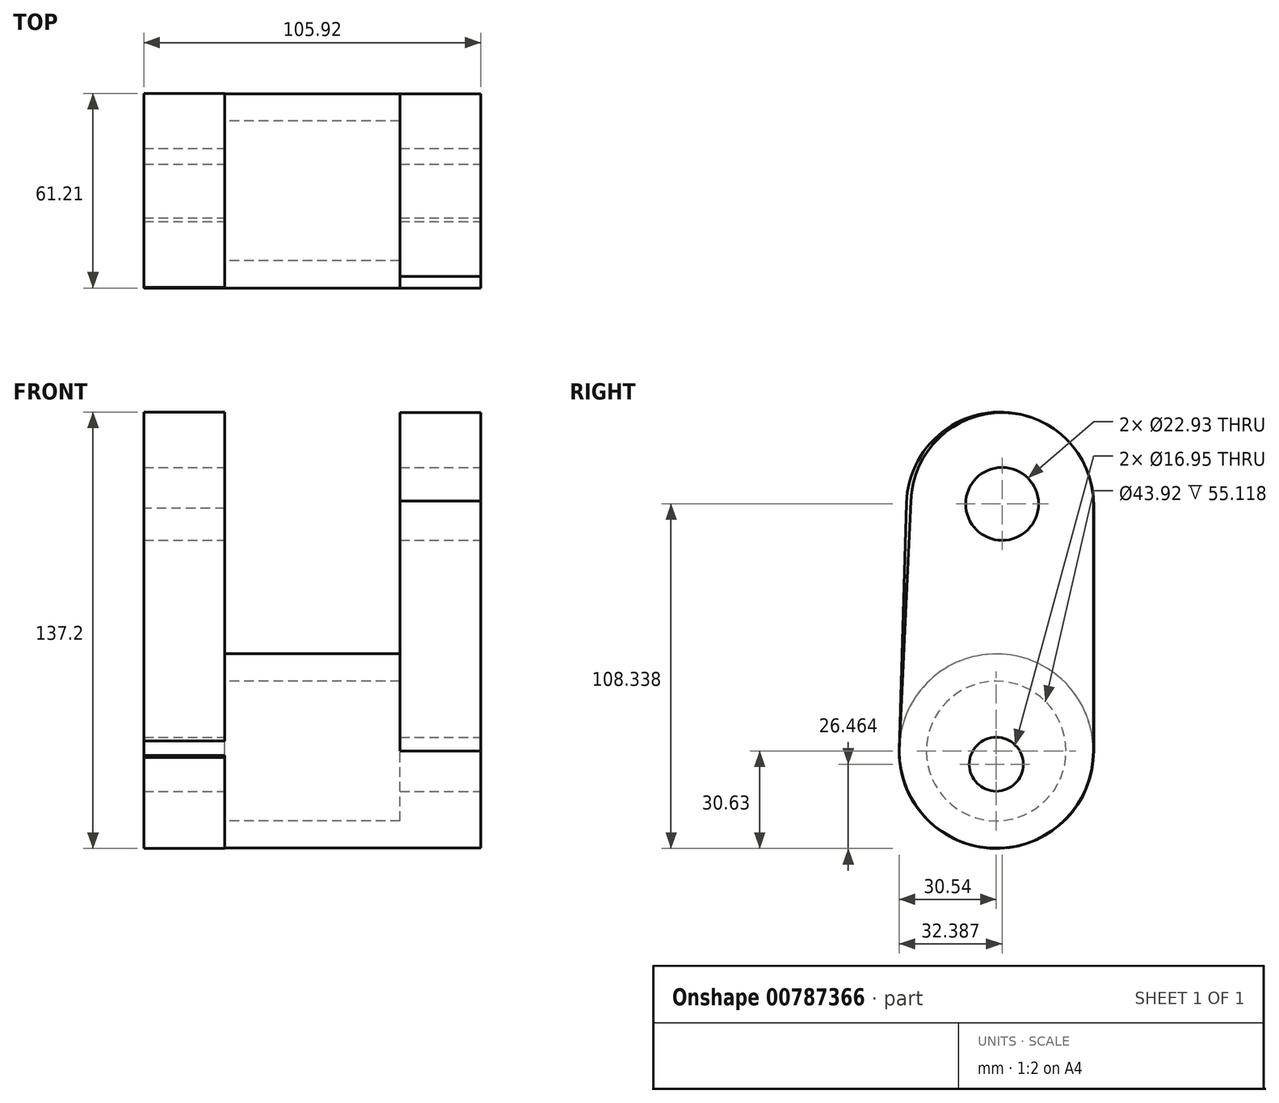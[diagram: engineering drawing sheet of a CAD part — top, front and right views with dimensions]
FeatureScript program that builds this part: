
annotation { "Feature Type Name" : "Feature", "Feature Type Description" : "" }
export const myFeature = defineFeature(function(context is Context, id is Id, definition is map)
    precondition{}
    {
        {
            var Q0;
            Q0=qCreatedBy(makeId("Right.planeOp"),FACE);
            var sketch = newSketch(context, id + "F0", { "sketchPlane" : qUnion([Q0])});
            skCircle(sketch, "E0", {"center": v(0, 0) * mm, "radius": 30.54 * mm});
            skCircle(sketch, "E1", {"center": v(0, 0) * mm, "radius": 21.96 * mm});
            skSolve(sketch);
        }
        {
            var Q0;
            Q0 = qSketchRegion(id + "F0", true);
            extrude(context, id + "F1", {"entities" : qUnion([Q0]), "depth" : 80.52 * mm, "offsetDistance" : 25.4 * mm});
        }
        {
            var Q0;
            Q0=qCreatedBy(makeId("Right.planeOp"),FACE);
            var sketch = newSketch(context, id + "F2", { "sketchPlane" : qUnion([Q0])});
            skLineSegment(sketch, "E2", {"start": v(30.66, 0) * mm, "end": v(30.66, 76.34) * mm});
            skLineSegment(sketch, "E3", {"start": v(-30.53, -2.07) * mm, "end": v(-28.22, 77.98) * mm});
            skArc(sketch, "E4", {"start": v(30.66, 76.34) * mm, "mid": v(2.04, 106.56) * mm, "end": v(-28.22, 77.98) * mm});
            skArc(sketch, "E5", {"start": v(-30.53, -2.07) * mm, "mid": v(1.06, -30.61) * mm, "end": v(30.66, 0) * mm});
            skSolve(sketch);
        }
        {
            var Q0;
            Q0 = qSketchRegion(id + "F2", true);
            extrude(context, id + "F3", {"entities" : qUnion([Q0]), "operationType" : NewBodyOperationType.ADD, "depth" : 25.4 * mm, "offsetDistance" : 25.4 * mm});
        }
        {
            var Q0;
            Q0=makeQuery(id+"F1.opExtrude","CAP_FACE",FACE,{"disambiguationData":[OSD([sQuery(id+"F0.wireOp",EDGE,"E0"),sQuery(id+"F0.wireOp",EDGE,"E1")])],"isStart":false});
            var sketch = newSketch(context, id + "F4", { "sketchPlane" : qUnion([Q0])});
            skLineSegment(sketch, "E6", {"start": v(-30.54, 0) * mm, "end": v(-26.83, 78.63) * mm});
            skLineSegment(sketch, "E7", {"start": v(30.54, 0) * mm, "end": v(30.54, 77.7) * mm});
            skArc(sketch, "E8", {"start": v(30.54, 77.7) * mm, "mid": v(2.3, 106.4) * mm, "end": v(-26.83, 78.63) * mm});
            skArc(sketch, "E9", {"start": v(-30.54, 0) * mm, "mid": v(0, -30.54) * mm, "end": v(30.54, 0) * mm});
            skSolve(sketch);
        }
        {
            var Q0;
            Q0 = qSketchRegion(id + "F4", true);
            extrude(context, id + "F5", {"entities" : qUnion([Q0]), "operationType" : NewBodyOperationType.ADD, "depth" : 25.4 * mm, "offsetDistance" : 25.4 * mm});
        }
        {
            var Q0;
            Q0=qCreatedBy(makeId("Right.planeOp"),FACE);
            var sketch = newSketch(context, id + "F6", { "sketchPlane" : qUnion([Q0])});
            skCircle(sketch, "E10", {"center": v(0, 0) * mm, "radius": 18.2 * mm});
            skCircle(sketch, "E11", {"center": v(0, 80.08) * mm, "radius": 16.93 * mm});
            skSolve(sketch);
        }
        {
            var Q0;
            Q0 = qSketchRegion(id + "F6", true);
            var Q1;
            Q1 = qSketchRegion(id + "F8", true);
            extrude(context, id + "F7", {"entities" : qUnion([Q0, Q1]), "operationType" : NewBodyOperationType.ADD, "depth" : 24.38 * mm, "offsetDistance" : 25.4 * mm});
        }
        {
            var Q0;
            Q0=makeQuery(id+"F5.opExtrude","CAP_FACE",FACE,{"disambiguationData":[OSD([sQuery(id+"F4.wireOp",EDGE,"E6"),sQuery(id+"F4.wireOp",EDGE,"E7"),sQuery(id+"F4.wireOp",EDGE,"E8"),sQuery(id+"F4.wireOp",EDGE,"E9")])],"isStart":false});
            var sketch = newSketch(context, id + "F8", { "sketchPlane" : qUnion([Q0])});
            skCircle(sketch, "E12", {"center": v(0, 83.16) * mm, "radius": 17.7 * mm});
            skCircle(sketch, "E13", {"center": v(0, 4.73) * mm, "radius": 19.06 * mm});
            skSolve(sketch);
        }
        {
            var Q0;
            Q0 = qSketchRegion(id + "F8", true);
            extrude(context, id + "F9", {"entities" : qUnion([Q0]), "operationType" : NewBodyOperationType.ADD, "oppositeDirection" : true, "depth" : 24.64 * mm, "offsetDistance" : 25.4 * mm});
        }
        {
            var Q0;
            Q0=makeQuery(id+"F5.opExtrude","CAP_FACE",FACE,{"disambiguationData":[OSD([sQuery(id+"F4.wireOp",EDGE,"E6"),sQuery(id+"F4.wireOp",EDGE,"E7"),sQuery(id+"F4.wireOp",EDGE,"E8"),sQuery(id+"F4.wireOp",EDGE,"E9")])],"isStart":false});
            var sketch = newSketch(context, id + "F10", { "sketchPlane" : qUnion([Q0])});
            skCircle(sketch, "E14", {"center": v(1.85, 77.7) * mm, "radius": 11.46 * mm});
            skSolve(sketch);
        }
        {
            var Q0;
            Q0=makeQuery(id+"F10.imprint","IMPRINT",FACE,{"disambiguationData":[TD([[makeQuery(id+"F10.imprint","IMPRINT",EDGE,{"derivedFrom":sQuery(id+"F10.wireOp",EDGE,"E14")}),1.0]])]});
            extrude(context, id + "F11", {"entities" : qUnion([Q0]), "operationType" : NewBodyOperationType.REMOVE, "oppositeDirection" : true, "depth" : 317.25 * mm, "offsetDistance" : 25.4 * mm});
        }
        {
            var Q0;
            Q0=makeQuery(id+"F5.opExtrude","CAP_FACE",FACE,{"disambiguationData":[OSD([sQuery(id+"F4.wireOp",EDGE,"E6"),sQuery(id+"F4.wireOp",EDGE,"E7"),sQuery(id+"F4.wireOp",EDGE,"E8"),sQuery(id+"F4.wireOp",EDGE,"E9")])],"isStart":false});
            var sketch = newSketch(context, id + "F12", { "sketchPlane" : qUnion([Q0])});
            skCircle(sketch, "E15", {"center": v(0, -4.17) * mm, "radius": 8.48 * mm});
            skSolve(sketch);
        }
        {
            var Q0;
            Q0=makeQuery(id+"F12.imprint","IMPRINT",FACE,{"disambiguationData":[TD([[makeQuery(id+"F12.imprint","IMPRINT",EDGE,{"derivedFrom":sQuery(id+"F12.wireOp",EDGE,"E15")}),1.0]])]});
            extrude(context, id + "F13", {"entities" : qUnion([Q0]), "operationType" : NewBodyOperationType.REMOVE, "oppositeDirection" : true, "depth" : 402.08 * mm, "offsetDistance" : 25.4 * mm});
        }
    });
